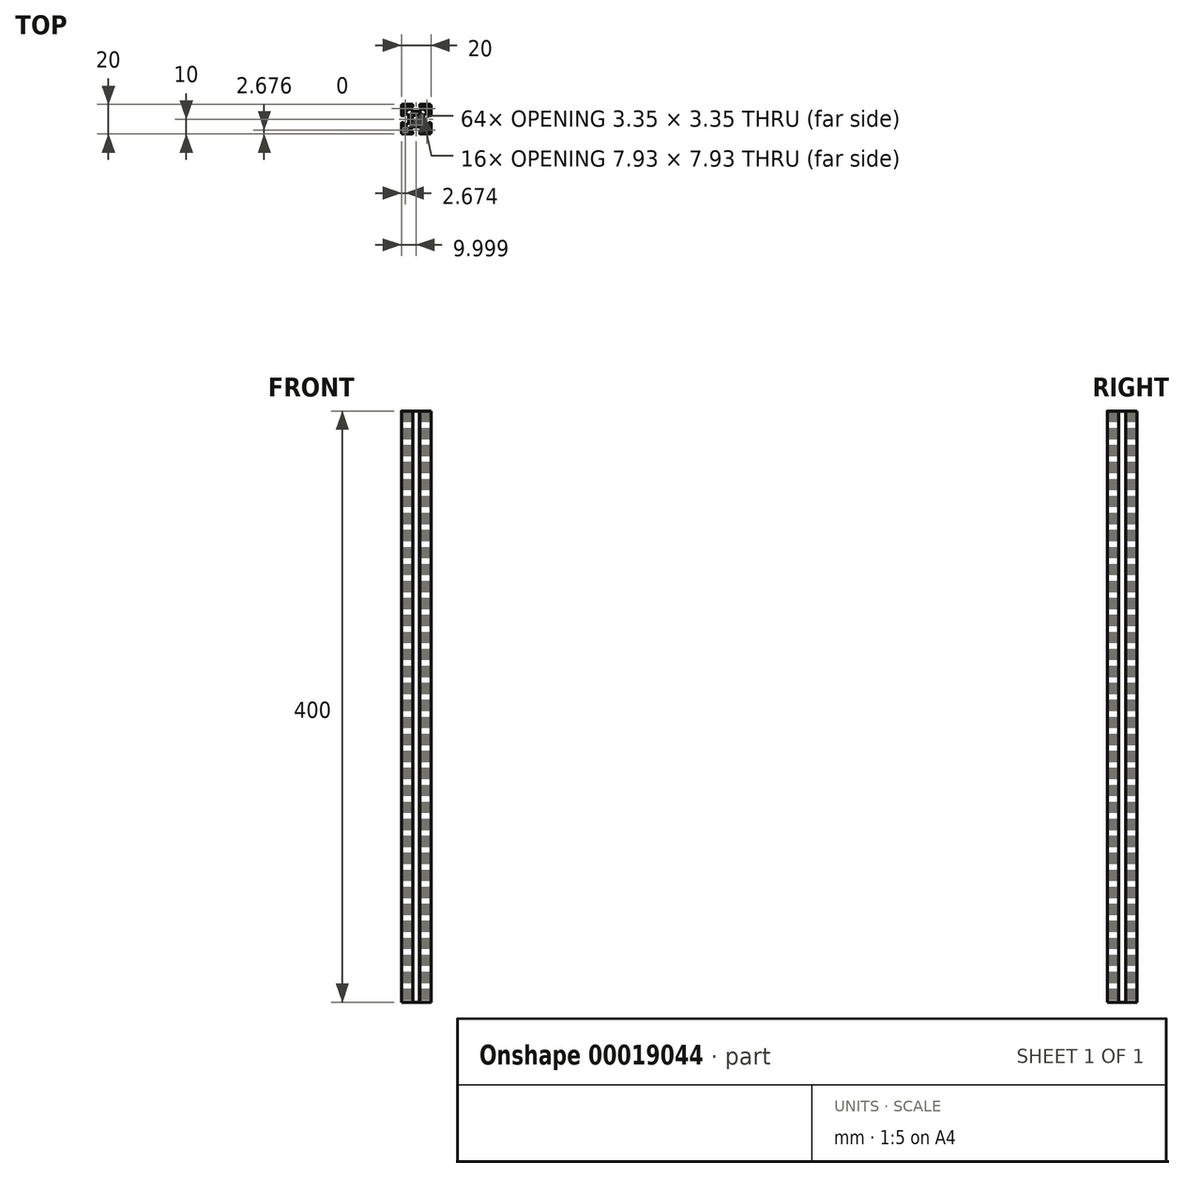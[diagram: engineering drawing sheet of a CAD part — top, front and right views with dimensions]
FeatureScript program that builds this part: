
annotation { "Feature Type Name" : "Feature", "Feature Type Description" : "" }
export const myFeature = defineFeature(function(context is Context, id is Id, definition is map)
    precondition{}
    {
        {
            var Q0;
            Q0=qCreatedBy(makeId("Top.planeOp"),FACE);
            var sketch = newSketch(context, id + "F0", { "sketchPlane" : qUnion([Q0])});
            skLineSegment(sketch, "E0", {"start": v(-770.66, 200.22) * mm, "end": v(-777.22, 200.22) * mm});
            skLineSegment(sketch, "E1", {"start": v(-770.66, 180.22) * mm, "end": v(-777.22, 180.22) * mm});
            skLineSegment(sketch, "E2", {"start": v(-769.86, 199.42) * mm, "end": v(-769.86, 192.86) * mm});
            skLineSegment(sketch, "E3", {"start": v(-789.86, 199.42) * mm, "end": v(-789.86, 192.86) * mm});
            skLineSegment(sketch, "E4", {"start": v(-777.5, 195.42) * mm, "end": v(-782.21, 195.42) * mm});
            skArc(sketch, "E5", {"start": v(-777.22, 200.22) * mm, "mid": v(-777.39, 200.15) * mm, "end": v(-777.46, 199.98) * mm});
            skLineSegment(sketch, "E6", {"start": v(-775.06, 198.62) * mm, "end": v(-777.22, 198.62) * mm});
            skArc(sketch, "E7", {"start": v(-777.46, 198.86) * mm, "mid": v(-777.39, 198.7) * mm, "end": v(-777.22, 198.62) * mm});
            skLineSegment(sketch, "E8", {"start": v(-782.5, 198.62) * mm, "end": v(-784.66, 198.62) * mm});
            skArc(sketch, "E9", {"start": v(-782.5, 198.62) * mm, "mid": v(-782.33, 198.7) * mm, "end": v(-782.26, 198.86) * mm});
            skLineSegment(sketch, "E10", {"start": v(-784.66, 197.87) * mm, "end": v(-784.66, 198.62) * mm});
            skLineSegment(sketch, "E11", {"start": v(-775.06, 197.87) * mm, "end": v(-775.06, 198.62) * mm});
            skLineSegment(sketch, "E12", {"start": v(-782.26, 198.86) * mm, "end": v(-782.26, 199.98) * mm});
            skArc(sketch, "E13", {"start": v(-782.26, 199.98) * mm, "mid": v(-782.33, 200.15) * mm, "end": v(-782.5, 200.22) * mm});
            skLineSegment(sketch, "E14", {"start": v(-777.46, 198.86) * mm, "end": v(-777.46, 199.98) * mm});
            skLineSegment(sketch, "E15", {"start": v(-782.21, 195.42) * mm, "end": v(-784.66, 197.87) * mm});
            skLineSegment(sketch, "E16", {"start": v(-777.5, 195.42) * mm, "end": v(-775.06, 197.87) * mm});
            skLineSegment(sketch, "E17", {"start": v(-777.5, 185.02) * mm, "end": v(-782.21, 185.02) * mm});
            skArc(sketch, "E18", {"start": v(-777.46, 180.46) * mm, "mid": v(-777.39, 180.3) * mm, "end": v(-777.22, 180.22) * mm});
            skLineSegment(sketch, "E19", {"start": v(-775.06, 181.82) * mm, "end": v(-777.22, 181.82) * mm});
            skArc(sketch, "E20", {"start": v(-777.22, 181.82) * mm, "mid": v(-777.39, 181.75) * mm, "end": v(-777.46, 181.58) * mm});
            skLineSegment(sketch, "E21", {"start": v(-782.5, 181.82) * mm, "end": v(-784.66, 181.82) * mm});
            skArc(sketch, "E22", {"start": v(-782.26, 181.58) * mm, "mid": v(-782.33, 181.75) * mm, "end": v(-782.5, 181.82) * mm});
            skLineSegment(sketch, "E23", {"start": v(-784.66, 182.57) * mm, "end": v(-784.66, 181.82) * mm});
            skLineSegment(sketch, "E24", {"start": v(-775.06, 182.57) * mm, "end": v(-775.06, 181.82) * mm});
            skLineSegment(sketch, "E25", {"start": v(-782.26, 181.58) * mm, "end": v(-782.26, 180.46) * mm});
            skArc(sketch, "E26", {"start": v(-782.5, 180.22) * mm, "mid": v(-782.33, 180.3) * mm, "end": v(-782.26, 180.46) * mm});
            skLineSegment(sketch, "E27", {"start": v(-777.46, 181.58) * mm, "end": v(-777.46, 180.46) * mm});
            skLineSegment(sketch, "E28", {"start": v(-782.21, 185.02) * mm, "end": v(-784.66, 182.57) * mm});
            skLineSegment(sketch, "E29", {"start": v(-777.5, 185.02) * mm, "end": v(-775.06, 182.57) * mm});
            skLineSegment(sketch, "E30", {"start": v(-774.66, 187.87) * mm, "end": v(-774.66, 192.57) * mm});
            skArc(sketch, "E31", {"start": v(-769.86, 187.58) * mm, "mid": v(-769.93, 187.75) * mm, "end": v(-770.1, 187.82) * mm});
            skLineSegment(sketch, "E32", {"start": v(-771.46, 185.42) * mm, "end": v(-771.46, 187.58) * mm});
            skArc(sketch, "E33", {"start": v(-771.22, 187.82) * mm, "mid": v(-771.39, 187.75) * mm, "end": v(-771.46, 187.58) * mm});
            skLineSegment(sketch, "E34", {"start": v(-771.46, 192.86) * mm, "end": v(-771.46, 195.02) * mm});
            skArc(sketch, "E35", {"start": v(-771.46, 192.86) * mm, "mid": v(-771.39, 192.7) * mm, "end": v(-771.22, 192.62) * mm});
            skLineSegment(sketch, "E36", {"start": v(-772.21, 195.02) * mm, "end": v(-771.46, 195.02) * mm});
            skLineSegment(sketch, "E37", {"start": v(-772.21, 185.42) * mm, "end": v(-771.46, 185.42) * mm});
            skLineSegment(sketch, "E38", {"start": v(-771.22, 192.62) * mm, "end": v(-770.1, 192.62) * mm});
            skArc(sketch, "E39", {"start": v(-770.1, 192.62) * mm, "mid": v(-769.93, 192.7) * mm, "end": v(-769.86, 192.86) * mm});
            skLineSegment(sketch, "E40", {"start": v(-771.22, 187.82) * mm, "end": v(-770.1, 187.82) * mm});
            skLineSegment(sketch, "E41", {"start": v(-774.66, 192.57) * mm, "end": v(-772.21, 195.02) * mm});
            skLineSegment(sketch, "E42", {"start": v(-774.66, 187.87) * mm, "end": v(-772.21, 185.42) * mm});
            skArc(sketch, "E43", {"start": v(-778.63, 192.65) * mm, "mid": v(-779.86, 192.94) * mm, "end": v(-781.09, 192.65) * mm});
            skArc(sketch, "E44", {"start": v(-782.29, 191.45) * mm, "mid": v(-782.58, 190.22) * mm, "end": v(-782.29, 188.99) * mm});
            skArc(sketch, "E45", {"start": v(-781.09, 187.8) * mm, "mid": v(-779.86, 187.5) * mm, "end": v(-778.63, 187.8) * mm});
            skArc(sketch, "E46", {"start": v(-778.35, 187.75) * mm, "mid": v(-778.48, 187.82) * mm, "end": v(-778.63, 187.8) * mm});
            skArc(sketch, "E47", {"start": v(-778.63, 192.65) * mm, "mid": v(-778.48, 192.62) * mm, "end": v(-778.35, 192.69) * mm});
            skArc(sketch, "E48", {"start": v(-777.43, 188.99) * mm, "mid": v(-777.14, 190.22) * mm, "end": v(-777.43, 191.45) * mm});
            skArc(sketch, "E49", {"start": v(-777.43, 188.99) * mm, "mid": v(-777.46, 188.84) * mm, "end": v(-777.39, 188.71) * mm});
            skArc(sketch, "E50", {"start": v(-777.39, 191.73) * mm, "mid": v(-777.46, 191.6) * mm, "end": v(-777.43, 191.45) * mm});
            skLineSegment(sketch, "E51", {"start": v(-777.39, 191.73) * mm, "end": v(-777, 192.12) * mm});
            skLineSegment(sketch, "E52", {"start": v(-778.35, 192.69) * mm, "end": v(-777.95, 193.09) * mm});
            skLineSegment(sketch, "E53", {"start": v(-778.35, 187.75) * mm, "end": v(-777.95, 187.35) * mm});
            skLineSegment(sketch, "E54", {"start": v(-777.39, 188.71) * mm, "end": v(-777, 188.32) * mm});
            skArc(sketch, "E55", {"start": v(-777, 192.12) * mm, "mid": v(-776.18, 193.9) * mm, "end": v(-777.95, 193.09) * mm});
            skArc(sketch, "E56", {"start": v(-777.95, 187.35) * mm, "mid": v(-776.18, 186.54) * mm, "end": v(-777, 188.32) * mm});
            skArc(sketch, "E57", {"start": v(-781.09, 187.8) * mm, "mid": v(-781.24, 187.82) * mm, "end": v(-781.37, 187.75) * mm});
            skArc(sketch, "E58", {"start": v(-781.37, 192.69) * mm, "mid": v(-781.24, 192.62) * mm, "end": v(-781.09, 192.65) * mm});
            skArc(sketch, "E59", {"start": v(-782.33, 188.71) * mm, "mid": v(-782.26, 188.84) * mm, "end": v(-782.29, 188.99) * mm});
            skArc(sketch, "E60", {"start": v(-782.29, 191.45) * mm, "mid": v(-782.26, 191.6) * mm, "end": v(-782.33, 191.73) * mm});
            skLineSegment(sketch, "E61", {"start": v(-782.33, 191.73) * mm, "end": v(-782.73, 192.12) * mm});
            skLineSegment(sketch, "E62", {"start": v(-781.37, 187.75) * mm, "end": v(-781.76, 187.35) * mm});
            skLineSegment(sketch, "E63", {"start": v(-782.33, 188.71) * mm, "end": v(-782.73, 188.32) * mm});
            skArc(sketch, "E64", {"start": v(-781.76, 193.09) * mm, "mid": v(-783.54, 193.9) * mm, "end": v(-782.73, 192.12) * mm});
            skArc(sketch, "E65", {"start": v(-782.73, 188.32) * mm, "mid": v(-783.54, 186.54) * mm, "end": v(-781.76, 187.35) * mm});
            skLineSegment(sketch, "E66", {"start": v(-781.37, 192.69) * mm, "end": v(-781.76, 193.09) * mm});
            skLineSegment(sketch, "E67", {"start": v(-773.87, 198.26) * mm, "end": v(-773.41, 197.8) * mm});
            skLineSegment(sketch, "E68", {"start": v(-772.28, 196.67) * mm, "end": v(-771.82, 196.2) * mm});
            skLineSegment(sketch, "E69", {"start": v(-770.86, 198.02) * mm, "end": v(-770.86, 196.6) * mm});
            skLineSegment(sketch, "E70", {"start": v(-772.06, 199.22) * mm, "end": v(-773.48, 199.22) * mm});
            skArc(sketch, "E71", {"start": v(-770.86, 198.02) * mm, "mid": v(-771.21, 198.87) * mm, "end": v(-772.06, 199.22) * mm});
            skLineSegment(sketch, "E72", {"start": v(-773.41, 197.8) * mm, "end": v(-773.98, 197.23) * mm});
            skLineSegment(sketch, "E73", {"start": v(-772.28, 196.67) * mm, "end": v(-772.84, 196.1) * mm});
            skArc(sketch, "E74", {"start": v(-773.98, 197.23) * mm, "mid": v(-773.98, 196.1) * mm, "end": v(-772.84, 196.1) * mm});
            skArc(sketch, "E75", {"start": v(-771.82, 196.2) * mm, "mid": v(-771.2, 196.08) * mm, "end": v(-770.86, 196.6) * mm});
            skArc(sketch, "E76", {"start": v(-773.48, 199.22) * mm, "mid": v(-774, 198.87) * mm, "end": v(-773.87, 198.26) * mm});
            skLineSegment(sketch, "E77", {"start": v(-773.87, 182.18) * mm, "end": v(-773.41, 182.64) * mm});
            skLineSegment(sketch, "E78", {"start": v(-772.28, 183.77) * mm, "end": v(-771.82, 184.23) * mm});
            skLineSegment(sketch, "E79", {"start": v(-770.86, 182.42) * mm, "end": v(-770.86, 183.84) * mm});
            skLineSegment(sketch, "E80", {"start": v(-772.06, 181.22) * mm, "end": v(-773.48, 181.22) * mm});
            skArc(sketch, "E81", {"start": v(-772.06, 181.22) * mm, "mid": v(-771.21, 181.57) * mm, "end": v(-770.86, 182.42) * mm});
            skLineSegment(sketch, "E82", {"start": v(-773.41, 182.64) * mm, "end": v(-773.98, 183.2) * mm});
            skLineSegment(sketch, "E83", {"start": v(-772.28, 183.77) * mm, "end": v(-772.84, 184.34) * mm});
            skArc(sketch, "E84", {"start": v(-772.84, 184.34) * mm, "mid": v(-773.98, 184.34) * mm, "end": v(-773.98, 183.2) * mm});
            skArc(sketch, "E85", {"start": v(-770.86, 183.84) * mm, "mid": v(-771.2, 184.36) * mm, "end": v(-771.82, 184.23) * mm});
            skArc(sketch, "E86", {"start": v(-773.87, 182.18) * mm, "mid": v(-774, 181.57) * mm, "end": v(-773.48, 181.22) * mm});
            skLineSegment(sketch, "E87", {"start": v(-785.06, 187.87) * mm, "end": v(-785.06, 192.57) * mm});
            skArc(sketch, "E88", {"start": v(-789.62, 187.82) * mm, "mid": v(-789.79, 187.75) * mm, "end": v(-789.86, 187.58) * mm});
            skLineSegment(sketch, "E89", {"start": v(-788.26, 185.42) * mm, "end": v(-788.26, 187.58) * mm});
            skArc(sketch, "E90", {"start": v(-788.26, 187.58) * mm, "mid": v(-788.33, 187.75) * mm, "end": v(-788.5, 187.82) * mm});
            skLineSegment(sketch, "E91", {"start": v(-788.26, 192.86) * mm, "end": v(-788.26, 195.02) * mm});
            skArc(sketch, "E92", {"start": v(-788.5, 192.62) * mm, "mid": v(-788.33, 192.7) * mm, "end": v(-788.26, 192.86) * mm});
            skLineSegment(sketch, "E93", {"start": v(-787.5, 195.02) * mm, "end": v(-788.26, 195.02) * mm});
            skLineSegment(sketch, "E94", {"start": v(-787.5, 185.42) * mm, "end": v(-788.26, 185.42) * mm});
            skLineSegment(sketch, "E95", {"start": v(-788.5, 192.62) * mm, "end": v(-789.62, 192.62) * mm});
            skArc(sketch, "E96", {"start": v(-789.86, 192.86) * mm, "mid": v(-789.79, 192.7) * mm, "end": v(-789.62, 192.62) * mm});
            skLineSegment(sketch, "E97", {"start": v(-788.5, 187.82) * mm, "end": v(-789.62, 187.82) * mm});
            skLineSegment(sketch, "E98", {"start": v(-785.06, 192.57) * mm, "end": v(-787.5, 195.02) * mm});
            skLineSegment(sketch, "E99", {"start": v(-785.06, 187.87) * mm, "end": v(-787.5, 185.42) * mm});
            skLineSegment(sketch, "E100", {"start": v(-769.86, 187.58) * mm, "end": v(-769.86, 181.02) * mm});
            skLineSegment(sketch, "E101", {"start": v(-782.5, 200.22) * mm, "end": v(-789.06, 200.22) * mm});
            skLineSegment(sketch, "E102", {"start": v(-789.86, 187.58) * mm, "end": v(-789.86, 181.02) * mm});
            skLineSegment(sketch, "E103", {"start": v(-782.5, 180.22) * mm, "end": v(-789.06, 180.22) * mm});
            skLineSegment(sketch, "E104", {"start": v(-785.84, 198.26) * mm, "end": v(-786.3, 197.8) * mm});
            skLineSegment(sketch, "E105", {"start": v(-787.44, 196.67) * mm, "end": v(-787.9, 196.2) * mm});
            skLineSegment(sketch, "E106", {"start": v(-788.86, 198.02) * mm, "end": v(-788.86, 196.6) * mm});
            skLineSegment(sketch, "E107", {"start": v(-787.66, 199.22) * mm, "end": v(-786.24, 199.22) * mm});
            skArc(sketch, "E108", {"start": v(-787.66, 199.22) * mm, "mid": v(-788.5, 198.87) * mm, "end": v(-788.86, 198.02) * mm});
            skLineSegment(sketch, "E109", {"start": v(-786.3, 197.8) * mm, "end": v(-785.74, 197.23) * mm});
            skLineSegment(sketch, "E110", {"start": v(-787.44, 196.67) * mm, "end": v(-786.87, 196.1) * mm});
            skArc(sketch, "E111", {"start": v(-786.87, 196.1) * mm, "mid": v(-785.74, 196.1) * mm, "end": v(-785.74, 197.23) * mm});
            skArc(sketch, "E112", {"start": v(-788.86, 196.6) * mm, "mid": v(-788.51, 196.08) * mm, "end": v(-787.9, 196.2) * mm});
            skArc(sketch, "E113", {"start": v(-785.84, 198.26) * mm, "mid": v(-785.72, 198.87) * mm, "end": v(-786.24, 199.22) * mm});
            skLineSegment(sketch, "E114", {"start": v(-785.84, 182.18) * mm, "end": v(-786.3, 182.64) * mm});
            skLineSegment(sketch, "E115", {"start": v(-787.44, 183.77) * mm, "end": v(-787.9, 184.23) * mm});
            skLineSegment(sketch, "E116", {"start": v(-788.86, 182.42) * mm, "end": v(-788.86, 183.84) * mm});
            skLineSegment(sketch, "E117", {"start": v(-787.66, 181.22) * mm, "end": v(-786.24, 181.22) * mm});
            skArc(sketch, "E118", {"start": v(-788.86, 182.42) * mm, "mid": v(-788.5, 181.57) * mm, "end": v(-787.66, 181.22) * mm});
            skLineSegment(sketch, "E119", {"start": v(-786.3, 182.64) * mm, "end": v(-785.74, 183.2) * mm});
            skLineSegment(sketch, "E120", {"start": v(-787.44, 183.77) * mm, "end": v(-786.87, 184.34) * mm});
            skArc(sketch, "E121", {"start": v(-785.74, 183.2) * mm, "mid": v(-785.74, 184.34) * mm, "end": v(-786.87, 184.34) * mm});
            skArc(sketch, "E122", {"start": v(-787.9, 184.23) * mm, "mid": v(-788.51, 184.36) * mm, "end": v(-788.86, 183.84) * mm});
            skArc(sketch, "E123", {"start": v(-786.24, 181.22) * mm, "mid": v(-785.72, 181.57) * mm, "end": v(-785.84, 182.18) * mm});
            skArc(sketch, "E124", {"start": v(-769.86, 199.42) * mm, "mid": v(-770.1, 199.99) * mm, "end": v(-770.66, 200.22) * mm});
            skArc(sketch, "E125", {"start": v(-770.66, 180.22) * mm, "mid": v(-770.1, 180.45) * mm, "end": v(-769.86, 181.02) * mm});
            skArc(sketch, "E126", {"start": v(-789.86, 181.02) * mm, "mid": v(-789.62, 180.45) * mm, "end": v(-789.06, 180.22) * mm});
            skArc(sketch, "E127", {"start": v(-789.06, 200.22) * mm, "mid": v(-789.62, 199.99) * mm, "end": v(-789.86, 199.42) * mm});
            skCircle(sketch, "E128", {"center": v(-779.86, 190.22) * mm, "radius": 2.72 * mm});
            skSolve(sketch);
        }
        {
            var Q0;
            Q0=makeQuery(id+"F0.imprint","IMPRINT",FACE,{"disambiguationData":[TD([[makeQuery(id+"F0.imprint","IMPRINT",EDGE,{"derivedFrom":sQuery(id+"F0.wireOp",EDGE,"E0")}),1.0]])]});
            extrude(context, id + "F1", {"entities" : qUnion([Q0]), "depth" : 400 * mm});
        }
        {
            var Q0;
            Q0=makeQuery(id+"F1.opExtrude","SWEPT_BODY",BODY,{"disambiguationData":[OSD([sQuery(id+"F0.wireOp",EDGE,"E0"),sQuery(id+"F0.wireOp",EDGE,"E1"),sQuery(id+"F0.wireOp",EDGE,"E2"),sQuery(id+"F0.wireOp",EDGE,"E3"),sQuery(id+"F0.wireOp",EDGE,"6afbd2fd-b612-43b9-8476-fa36e6408dfa"),sQuery(id+"F0.wireOp",EDGE,"E4"),sQuery(id+"F0.wireOp",EDGE,"E5"),sQuery(id+"F0.wireOp",EDGE,"E6"),sQuery(id+"F0.wireOp",EDGE,"E7"),sQuery(id+"F0.wireOp",EDGE,"E8"),sQuery(id+"F0.wireOp",EDGE,"E9"),sQuery(id+"F0.wireOp",EDGE,"E10"),sQuery(id+"F0.wireOp",EDGE,"E11"),sQuery(id+"F0.wireOp",EDGE,"E12"),sQuery(id+"F0.wireOp",EDGE,"E13"),sQuery(id+"F0.wireOp",EDGE,"E14"),sQuery(id+"F0.wireOp",EDGE,"aec2d2fb-ca71-441a-a28b-dcb6cec08c7a"),sQuery(id+"F0.wireOp",EDGE,"f44804ff-6397-4be9-b25c-bdcd1cbdf786"),sQuery(id+"F0.wireOp",EDGE,"639aac7c-82c4-4d70-abd1-0655e23eadfe"),sQuery(id+"F0.wireOp",EDGE,"E15"),sQuery(id+"F0.wireOp",EDGE,"E16"),sQuery(id+"F0.wireOp",EDGE,"c2582b0c-8e8c-4916-ac5c-c4b849a6f876"),sQuery(id+"F0.wireOp",EDGE,"4422e690-65f8-4d57-8c17-023425b33ca7"),sQuery(id+"F0.wireOp",EDGE,"1d33335d-38ea-4350-b553-d3db465c2bd0"),sQuery(id+"F0.wireOp",EDGE,"E17"),sQuery(id+"F0.wireOp",EDGE,"8d6e34ac-a5d8-4c82-85b7-c46690091ffd"),sQuery(id+"F0.wireOp",EDGE,"E18"),sQuery(id+"F0.wireOp",EDGE,"E19"),sQuery(id+"F0.wireOp",EDGE,"E20"),sQuery(id+"F0.wireOp",EDGE,"E21"),sQuery(id+"F0.wireOp",EDGE,"E22"),sQuery(id+"F0.wireOp",EDGE,"E23"),sQuery(id+"F0.wireOp",EDGE,"E24"),sQuery(id+"F0.wireOp",EDGE,"E25"),sQuery(id+"F0.wireOp",EDGE,"E26"),sQuery(id+"F0.wireOp",EDGE,"E27"),sQuery(id+"F0.wireOp",EDGE,"E28"),sQuery(id+"F0.wireOp",EDGE,"E29"),sQuery(id+"F0.wireOp",EDGE,"a73d43c5-4739-48a6-b3d6-2bdba3c12938"),sQuery(id+"F0.wireOp",EDGE,"80bd6614-c644-4757-aa7d-39d03bbcfdec"),sQuery(id+"F0.wireOp",EDGE,"857f19c9-f5d2-49f9-ba00-a2bbe5d01ea3"),sQuery(id+"F0.wireOp",EDGE,"4f6a0bee-a0f5-45a4-8184-897b0fc4ab66"),sQuery(id+"F0.wireOp",EDGE,"bbec12ca-8425-48cb-ac52-f66a64ce9ce2"),sQuery(id+"F0.wireOp",EDGE,"77010181-1ce9-4eb5-b00f-63b9843d8d61"),sQuery(id+"F0.wireOp",EDGE,"969c7158-9ce4-40b5-b401-e35ff1d326f4"),sQuery(id+"F0.wireOp",EDGE,"E30"),sQuery(id+"F0.wireOp",EDGE,"E31"),sQuery(id+"F0.wireOp",EDGE,"E32"),sQuery(id+"F0.wireOp",EDGE,"E33"),sQuery(id+"F0.wireOp",EDGE,"E34"),sQuery(id+"F0.wireOp",EDGE,"E35"),sQuery(id+"F0.wireOp",EDGE,"E36"),sQuery(id+"F0.wireOp",EDGE,"E37"),sQuery(id+"F0.wireOp",EDGE,"E38"),sQuery(id+"F0.wireOp",EDGE,"E39"),sQuery(id+"F0.wireOp",EDGE,"E40"),sQuery(id+"F0.wireOp",EDGE,"E41"),sQuery(id+"F0.wireOp",EDGE,"E42"),sQuery(id+"F0.wireOp",EDGE,"7512f460-3dae-41ae-8bd3-e2205881c18d"),sQuery(id+"F0.wireOp",EDGE,"0011cfcd-5d99-4bf1-a6bf-62a3a8444d4d"),sQuery(id+"F0.wireOp",EDGE,"93abd8ed-0801-4c5a-b2d1-764bf78cd7a9"),sQuery(id+"F0.wireOp",EDGE,"2aa63244-e017-4f5b-ada5-1b099d09bebe"),sQuery(id+"F0.wireOp",EDGE,"992542c0-fcd2-46bd-8571-0cf53c8af5f4"),sQuery(id+"F0.wireOp",EDGE,"8190dde2-a3a1-4061-84ee-bd83539ad5bf"),sQuery(id+"F0.wireOp",EDGE,"E46"),sQuery(id+"F0.wireOp",EDGE,"E47"),sQuery(id+"F0.wireOp",EDGE,"E49"),sQuery(id+"F0.wireOp",EDGE,"E50"),sQuery(id+"F0.wireOp",EDGE,"E51"),sQuery(id+"F0.wireOp",EDGE,"E52"),sQuery(id+"F0.wireOp",EDGE,"E53"),sQuery(id+"F0.wireOp",EDGE,"E54"),sQuery(id+"F0.wireOp",EDGE,"E55"),sQuery(id+"F0.wireOp",EDGE,"E56"),sQuery(id+"F0.wireOp",EDGE,"E57"),sQuery(id+"F0.wireOp",EDGE,"E58"),sQuery(id+"F0.wireOp",EDGE,"E59"),sQuery(id+"F0.wireOp",EDGE,"E60"),sQuery(id+"F0.wireOp",EDGE,"E61"),sQuery(id+"F0.wireOp",EDGE,"E62"),sQuery(id+"F0.wireOp",EDGE,"E63"),sQuery(id+"F0.wireOp",EDGE,"E64"),sQuery(id+"F0.wireOp",EDGE,"E65"),sQuery(id+"F0.wireOp",EDGE,"E66"),sQuery(id+"F0.wireOp",EDGE,"E67"),sQuery(id+"F0.wireOp",EDGE,"E68"),sQuery(id+"F0.wireOp",EDGE,"E69"),sQuery(id+"F0.wireOp",EDGE,"E70"),sQuery(id+"F0.wireOp",EDGE,"E71"),sQuery(id+"F0.wireOp",EDGE,"E72"),sQuery(id+"F0.wireOp",EDGE,"E73"),sQuery(id+"F0.wireOp",EDGE,"E74"),sQuery(id+"F0.wireOp",EDGE,"E75"),sQuery(id+"F0.wireOp",EDGE,"E76"),sQuery(id+"F0.wireOp",EDGE,"E77"),sQuery(id+"F0.wireOp",EDGE,"E78"),sQuery(id+"F0.wireOp",EDGE,"E79"),sQuery(id+"F0.wireOp",EDGE,"E80"),sQuery(id+"F0.wireOp",EDGE,"E81"),sQuery(id+"F0.wireOp",EDGE,"E82"),sQuery(id+"F0.wireOp",EDGE,"E83"),sQuery(id+"F0.wireOp",EDGE,"E84"),sQuery(id+"F0.wireOp",EDGE,"E85"),sQuery(id+"F0.wireOp",EDGE,"E86"),sQuery(id+"F0.wireOp",EDGE,"E87"),sQuery(id+"F0.wireOp",EDGE,"8104d4e8-ae96-4528-972a-1b3496e05406"),sQuery(id+"F0.wireOp",EDGE,"E88"),sQuery(id+"F0.wireOp",EDGE,"E89"),sQuery(id+"F0.wireOp",EDGE,"E90"),sQuery(id+"F0.wireOp",EDGE,"E91"),sQuery(id+"F0.wireOp",EDGE,"E92"),sQuery(id+"F0.wireOp",EDGE,"E93"),sQuery(id+"F0.wireOp",EDGE,"E94"),sQuery(id+"F0.wireOp",EDGE,"E95"),sQuery(id+"F0.wireOp",EDGE,"E96"),sQuery(id+"F0.wireOp",EDGE,"E97"),sQuery(id+"F0.wireOp",EDGE,"E98"),sQuery(id+"F0.wireOp",EDGE,"E99"),sQuery(id+"F0.wireOp",EDGE,"206971a4-01ed-4f59-9d01-f6b68ac83e35"),sQuery(id+"F0.wireOp",EDGE,"1d0437db-7a86-4e28-a551-0de2fb162d59"),sQuery(id+"F0.wireOp",EDGE,"6e3b9de9-3dba-4990-86d5-19571cca6973"),sQuery(id+"F0.wireOp",EDGE,"658cff84-2528-4d56-a872-821425701e82"),sQuery(id+"F0.wireOp",EDGE,"906a624c-7afa-45cd-8700-fb7c27bb8abe"),sQuery(id+"F0.wireOp",EDGE,"d0e9cb90-56db-4401-9904-fc937a7186e5"),sQuery(id+"F0.wireOp",EDGE,"E100"),sQuery(id+"F0.wireOp",EDGE,"E101"),sQuery(id+"F0.wireOp",EDGE,"E102"),sQuery(id+"F0.wireOp",EDGE,"E103"),sQuery(id+"F0.wireOp",EDGE,"E104"),sQuery(id+"F0.wireOp",EDGE,"E105"),sQuery(id+"F0.wireOp",EDGE,"E106"),sQuery(id+"F0.wireOp",EDGE,"E107"),sQuery(id+"F0.wireOp",EDGE,"E108"),sQuery(id+"F0.wireOp",EDGE,"E109"),sQuery(id+"F0.wireOp",EDGE,"E110"),sQuery(id+"F0.wireOp",EDGE,"E111"),sQuery(id+"F0.wireOp",EDGE,"E112"),sQuery(id+"F0.wireOp",EDGE,"E113"),sQuery(id+"F0.wireOp",EDGE,"E114"),sQuery(id+"F0.wireOp",EDGE,"E115"),sQuery(id+"F0.wireOp",EDGE,"E116"),sQuery(id+"F0.wireOp",EDGE,"E117"),sQuery(id+"F0.wireOp",EDGE,"E118"),sQuery(id+"F0.wireOp",EDGE,"E119"),sQuery(id+"F0.wireOp",EDGE,"E120"),sQuery(id+"F0.wireOp",EDGE,"E121"),sQuery(id+"F0.wireOp",EDGE,"E122"),sQuery(id+"F0.wireOp",EDGE,"E123"),sQuery(id+"F0.wireOp",EDGE,"E124"),sQuery(id+"F0.wireOp",EDGE,"E125"),sQuery(id+"F0.wireOp",EDGE,"E126"),sQuery(id+"F0.wireOp",EDGE,"E127"),sQuery(id+"F0.wireOp",EDGE,"E128")])]});
            transform(context, id + "F2", {"entities" : qUnion([Q0]), "transformType" : TransformType.TRANSLATION_3D, "dx" : 780.97 * mm, "dy" : -188.54 * mm, "dz" : -211.27 * mm, "makeCopy" : false});
        }
        {
            var Q0;
            Q0=makeQuery(id+"F1.opExtrude","SWEPT_FACE",FACE,{"disambiguationData":[OSD([sQuery(id+"F0.wireOp",EDGE,"E2")])]});
            var sketch = newSketch(context, id + "F3", { "sketchPlane" : qUnion([Q0])});
            skPoint(sketch, "E129.0", {"position": v(11.68, 188.73) * mm});
            skPoint(sketch, "E129.1", {"position": v(-8.32, 188.73) * mm});
            skLineSegment(sketch, "E130", {"start": v(11.68, 188.73) * mm, "end": v(-8.32, 188.73) * mm, "construction": true});
            skLineSegment(sketch, "E131", {"start": v(11.68, 188.73) * mm, "end": v(11.68, 158.73) * mm, "construction": true});
            skLineSegment(sketch, "E132", {"start": v(-8.32, 188.73) * mm, "end": v(-8.32, 158.73) * mm, "construction": true});
            skLineSegment(sketch, "E133", {"start": v(-8.32, 158.73) * mm, "end": v(11.68, 158.73) * mm, "construction": true});
            skPoint(sketch, "E134.0", {"position": v(-8.32, -211.27) * mm});
            skPoint(sketch, "E134.1", {"position": v(11.68, -211.27) * mm});
            skLineSegment(sketch, "E135", {"start": v(-8.32, -211.27) * mm, "end": v(11.68, -211.27) * mm, "construction": true});
            skLineSegment(sketch, "E136", {"start": v(11.68, -211.27) * mm, "end": v(11.68, -181.27) * mm, "construction": true});
            skLineSegment(sketch, "E137", {"start": v(-8.32, -211.27) * mm, "end": v(-8.32, -181.27) * mm, "construction": true});
            skLineSegment(sketch, "E138", {"start": v(-8.32, -181.27) * mm, "end": v(11.68, -181.27) * mm, "construction": true});
            skLineSegment(sketch, "E139", {"start": v(-8.32, 178.73) * mm, "end": v(11.68, 178.73) * mm, "construction": true});
            skLineSegment(sketch, "E140", {"start": v(-8.32, -201.27) * mm, "end": v(11.68, -201.27) * mm, "construction": true});
            skSolve(sketch);
        }
        {
            var Q0;
            Q0=makeQuery(id+"F1.opExtrude","SWEPT_FACE",FACE,{"disambiguationData":[OSD([sQuery(id+"F0.wireOp",EDGE,"E3")])]});
            var sketch = newSketch(context, id + "F4", { "sketchPlane" : qUnion([Q0])});
            skLineSegment(sketch, "E141.0", {"start": v(8.32, -181.27) * mm, "end": v(-11.68, -181.27) * mm, "construction": true});
            skLineSegment(sketch, "E142.0", {"start": v(8.32, 158.73) * mm, "end": v(-11.68, 158.73) * mm, "construction": true});
            skLineSegment(sketch, "E143.0", {"start": v(8.32, 178.73) * mm, "end": v(-11.68, 178.73) * mm, "construction": true});
            skLineSegment(sketch, "E144.0", {"start": v(8.32, -201.27) * mm, "end": v(-11.68, -201.27) * mm, "construction": true});
            skSolve(sketch);
        }
        {
            var Q0;
            Q0=makeQuery(id+"F1.opExtrude","SWEPT_FACE",FACE,{"disambiguationData":[OSD([sQuery(id+"F0.wireOp",EDGE,"E103")])]});
            var sketch = newSketch(context, id + "F5", { "sketchPlane" : qUnion([Q0])});
            skPoint(sketch, "E145.0", {"position": v(-8.9, 158.73) * mm});
            skPoint(sketch, "E145.1", {"position": v(11.1, 158.73) * mm});
            skLineSegment(sketch, "E146", {"start": v(-8.9, 158.73) * mm, "end": v(11.1, 158.73) * mm, "construction": true});
            skPoint(sketch, "E147.0", {"position": v(-8.9, -181.27) * mm});
            skPoint(sketch, "E147.1", {"position": v(11.1, -181.27) * mm});
            skLineSegment(sketch, "E148", {"start": v(11.1, -181.27) * mm, "end": v(-8.9, -181.27) * mm, "construction": true});
            skPoint(sketch, "E149.0", {"position": v(-8.9, -201.27) * mm});
            skPoint(sketch, "E149.1", {"position": v(11.1, -201.27) * mm});
            skLineSegment(sketch, "E150", {"start": v(-8.9, -201.27) * mm, "end": v(11.1, -201.27) * mm, "construction": true});
            skPoint(sketch, "E151.0", {"position": v(-8.9, 178.73) * mm});
            skPoint(sketch, "E151.1", {"position": v(11.1, 178.73) * mm});
            skLineSegment(sketch, "E152", {"start": v(11.1, 178.73) * mm, "end": v(-8.9, 178.73) * mm, "construction": true});
            skSolve(sketch);
        }
        {
            var Q0;
            Q0=makeQuery(id+"F1.opExtrude","SWEPT_FACE",FACE,{"disambiguationData":[OSD([sQuery(id+"F0.wireOp",EDGE,"E0")])]});
            var sketch = newSketch(context, id + "F6", { "sketchPlane" : qUnion([Q0])});
            skLineSegment(sketch, "E153.0", {"start": v(8.9, 158.73) * mm, "end": v(-11.1, 158.73) * mm, "construction": true});
            skPoint(sketch, "E154.0", {"position": v(-11.1, -181.27) * mm});
            skPoint(sketch, "E154.1", {"position": v(8.9, -181.27) * mm});
            skLineSegment(sketch, "E155", {"start": v(-11.1, -181.27) * mm, "end": v(8.9, -181.27) * mm, "construction": true});
            skPoint(sketch, "E156.0", {"position": v(8.9, -201.27) * mm});
            skPoint(sketch, "E156.1", {"position": v(-11.1, -201.27) * mm});
            skLineSegment(sketch, "E157", {"start": v(8.9, -201.27) * mm, "end": v(-11.1, -201.27) * mm, "construction": true});
            skPoint(sketch, "E158.0", {"position": v(8.9, 178.73) * mm});
            skPoint(sketch, "E158.1", {"position": v(-11.1, 178.73) * mm});
            skLineSegment(sketch, "E159", {"start": v(8.9, 178.73) * mm, "end": v(-11.1, 178.73) * mm, "construction": true});
            skSolve(sketch);
        }
    });
